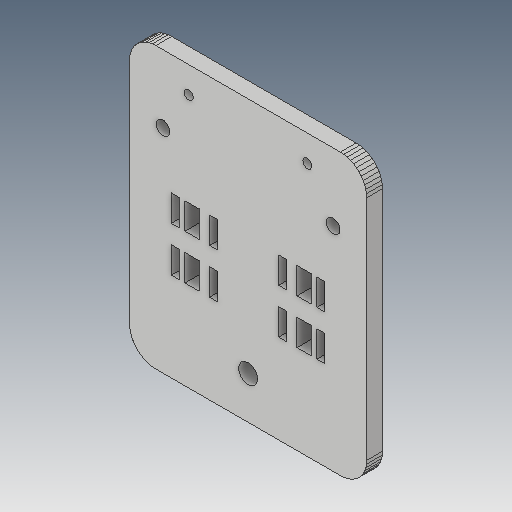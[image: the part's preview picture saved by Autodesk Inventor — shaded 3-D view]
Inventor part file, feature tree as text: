
AUTODESK INVENTOR PART (.ipt)
format: ipt  version: 2017 (Build 210142000, 142)  size: 375,296 bytes
history: native  units: mm
features: sketch x4, hole x3, extrude x1
ambient origin geometry x8: Origin, YZ Plane, XZ Plane, XY Plane, X Axis, Y Axis, Z Axis, Center Point
bodies: Solid1 (feature_tree)
feature tree (8):
  extrude  "Extrusion1"  Depth=6.0mm
  hole  "Hole1"  [1 undecoded]
  hole  "Hole2"  [1 undecoded]
  hole  "Hole3"  [1 undecoded]
  sketch  "Sketch1"  dims[d0=6.0mm d1=0.0mm]
  sketch  "Sketch2"  dims[d2=3.4mm d3=6.0mm d4=4.0mm d5=2.0mm d6=90.0deg d7=8.0mm d8=20.594885mm]
  sketch  "Sketch3"  dims[d9=5.2mm d10=6.0mm d11=4.0mm d12=2.0mm d13=90.0deg d14=8.0mm d15=20.594885mm]
  sketch  "Sketch4"  dims[d16=7.2mm d17=6.0mm d18=4.0mm d19=2.0mm d20=90.0deg d21=8.0mm d22=20.594885mm d23=1.0mm d24=1.0mm]
note: 3 required parameter values undecoded (feature->parameter linkage not recoverable at this tier; creation-order binding heuristic only, values carry confidence <= 0.55)
